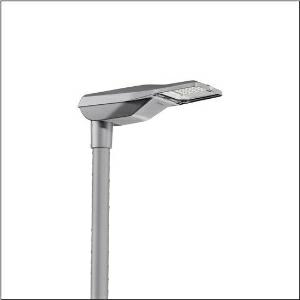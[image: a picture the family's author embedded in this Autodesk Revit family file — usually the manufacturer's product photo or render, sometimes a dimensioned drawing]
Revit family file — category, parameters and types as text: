
# Revit family: streetlight_sl_21_micro___st1_0a_5xe5d33a08cb_e1ea
name_source: partatom
category: Lighting Fixtures
units: mm (PartAtom-declared; Revit-internal decimal feet)

## family parameters
Cut with Voids When Loaded = No
Host = Face
Light Source = No
Part Type = Normal
Room Calculation Point = No
Round Connector Dimension = Use Diameter
Shared = No

## types (1)
- --- (1 x LED, 2290 lm, 15.8 W, 3000K)
    Apparent Load = 16 VA
    CIE Flux Codes = 37 72 97 100 100
    Color Rendering = 70
    Color Temperature = 3000K
    Default Elevation = 1800 mm
    Description = Streetlight SL 21 micro, mast luminaire, primary light control with lens, of PMMA, primary optical cover: cover, of toughened safety glass, transparent, light distribution: ST1.0a, light emission: direct distribution, primary light characteristic: asymmetric, installation type: side-entry, post-top, LED, 3G 1.5mm², High Power LED, rated luminous flux: 2.290lm, luminous efficacy: 145lm/W, light colour: 730, colour temperature: 3000K, control gear: Easy, control: flexible luminous flux parameterisation, time-dependent luminous flux control, constant luminous flux control, overheat protection, mains connection: 230..240V, AC, 50/60Hz, connection cable pre-assembled, cable length: 5,5m, wiring characteristics: H07RN-F, start of lifetime: 16W, end of service life: 16W, reduction: 9W, luminaire housing, of diecast aluminium, powder-coated, Siteco® metallic grey (DB 702S), corrosivity category C5 mid according to DIN EN ISO 12944, please order mast flange separately, inclination adjustable: 0°, 5°, 10°, 15°, sealing non-destructively replaceable, multi-level sealing system, length: 528mm, width: 235mm, height: 110mm, mast flange for spigot size: 42mm (side-entry): 5XC10008XM4, 60/48mm (side-entry/post-top): 5XC10108XM2, 76/60mm (side-entry/post-top): 5XC10108XM1, protection rating (complete): IP66, insulation class (complete): insulation class II (safety insulation), certification: CE, ENEC, ENEC+, VDE, impact resistance: IK10, permissible operating ambient temperature for outdoor applications: -40..+50°C, standard-compliant lighting for roads and squares, packaging unit: 1 piece

Light Distribution: ST1.0a
    Height = 110 mm
    Lamp = 1 x LED
    Lamp Light Flux = 2290 lm
    Lamp Power = 15.8 W
    Lamp count = 1
    Length = 528 mm
    Luminous efficacy = 145 lm/W
    Manufacturer = Siteco
    ModVariant = No
    Model = 5XE5D33A08CB
    Number of Poles = 1
    OnlyDefault = Yes
    Power Factor = 1
    Product Name = Streetlight SL 21 micro | ST1.0a
    Product group = mast luminaire | pylon top
    ProductGroupID = 6100
    Protection Class = Protection class II
    Protection Degree = IP 66
    RLX_Detail_Level = 1
    RLX_Emergency_Light_Flux = 0 lm
    RLX_Emergency_Type = 0
    RLX_Emergency_Type_DB = No
    RlxData = <blob elided: 97813 chars, md5=5d31c5c3>
    Socket = socket
    Standby Power = 0 W
    System Light Flux = 2290 lm
    System Power = 16 W
    Type Comments = factory setting: luminous flux: 100 % | Output Level: 100 % | 300 mA
    Type Image = l_1006881.jpg
    URL = http://relux.com
    VarID = @adj_177145
    Voltage = 0 V
    Weight = 0.00 kg
    Width = 235 mm

## geometry (parser evidence)
native form markers: Blend x4, Sweep x8
no freeform markers — native parametric forms only
